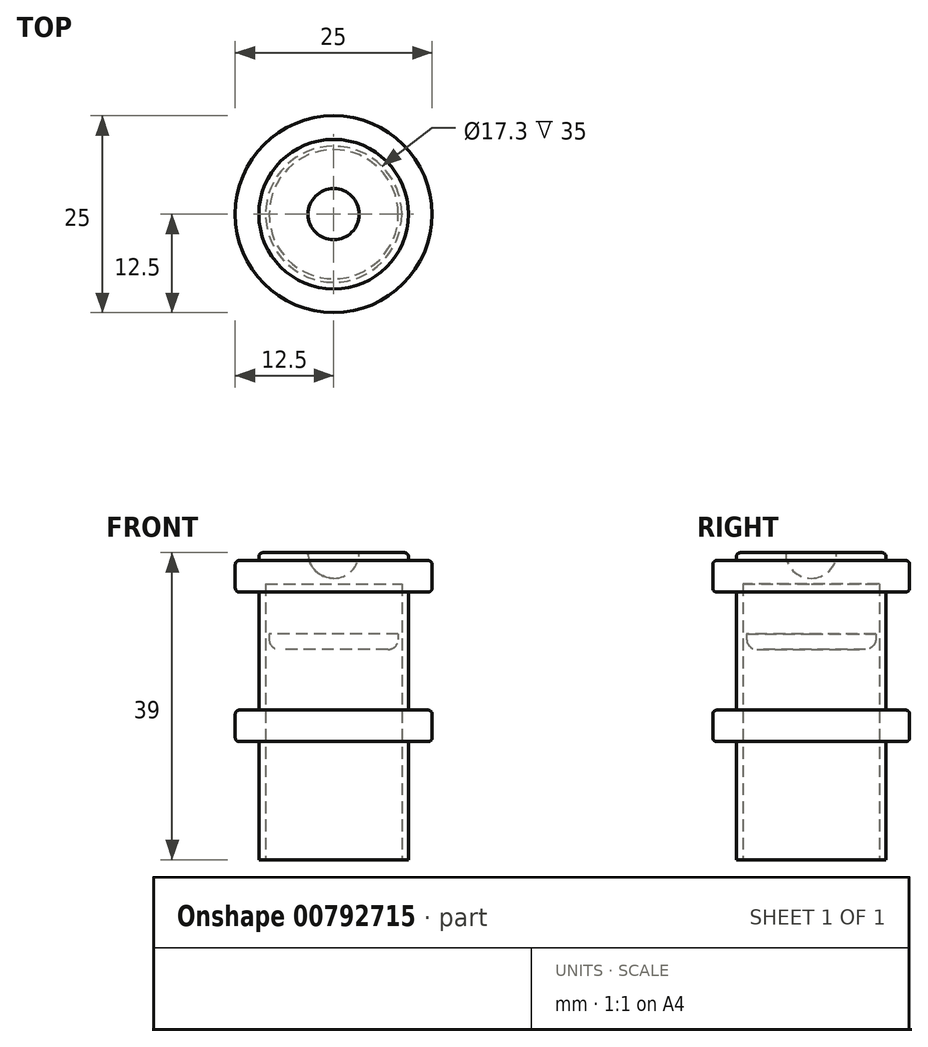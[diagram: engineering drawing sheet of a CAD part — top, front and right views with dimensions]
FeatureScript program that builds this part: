
annotation { "Feature Type Name" : "Feature", "Feature Type Description" : "" }
export const myFeature = defineFeature(function(context is Context, id is Id, definition is map)
    precondition{}
    {
        {
            var Q0;
            Q0=qCreatedBy(makeId("Front.planeOp"),FACE);
            var sketch = newSketch(context, id + "F0", { "sketchPlane" : qUnion([Q0])});
            skLineSegment(sketch, "E0", {"start": v(0, 0) * mm, "end": v(-9.5, 0) * mm});
            skLineSegment(sketch, "E1", {"start": v(-9.5, 0) * mm, "end": v(-9.5, 15) * mm});
            skLineSegment(sketch, "E2", {"start": v(-9.5, 15) * mm, "end": v(-12, 15) * mm});
            skLineSegment(sketch, "E3", {"start": v(-12.5, 15.5) * mm, "end": v(-12.5, 18.5) * mm});
            skLineSegment(sketch, "E4", {"start": v(-12, 19) * mm, "end": v(-9.5, 19) * mm});
            skLineSegment(sketch, "E5", {"start": v(-9.5, 19) * mm, "end": v(-9.5, 34) * mm});
            skLineSegment(sketch, "E6", {"start": v(-9.5, 34) * mm, "end": v(-12, 34) * mm});
            skLineSegment(sketch, "E7", {"start": v(-12.5, 34.5) * mm, "end": v(-12.5, 37.5) * mm});
            skLineSegment(sketch, "E8", {"start": v(-12, 38) * mm, "end": v(-9.5, 38) * mm});
            skLineSegment(sketch, "E9", {"start": v(-9.5, 38) * mm, "end": v(-9.5, 38.5) * mm});
            skLineSegment(sketch, "E10", {"start": v(-9, 39) * mm, "end": v(0, 39) * mm});
            skLineSegment(sketch, "E11", {"start": v(0, 39) * mm, "end": v(0, 0) * mm});
            skPoint(sketch, "E12.visualSharp", {"position": v(-12.5, 15) * mm});
            skArc(sketch, "E12.filletArc", {"start": v(-12.5, 15.5) * mm, "mid": v(-12.35, 15.15) * mm, "end": v(-12, 15) * mm});
            skPoint(sketch, "E13.visualSharp", {"position": v(-12.5, 19) * mm});
            skArc(sketch, "E13.filletArc", {"start": v(-12, 19) * mm, "mid": v(-12.35, 18.85) * mm, "end": v(-12.5, 18.5) * mm});
            skPoint(sketch, "E14.visualSharp", {"position": v(-12.5, 38) * mm});
            skArc(sketch, "E14.filletArc", {"start": v(-12, 38) * mm, "mid": v(-12.35, 37.85) * mm, "end": v(-12.5, 37.5) * mm});
            skPoint(sketch, "E15.visualSharp", {"position": v(-12.5, 34) * mm});
            skArc(sketch, "E15.filletArc", {"start": v(-12.5, 34.5) * mm, "mid": v(-12.35, 34.15) * mm, "end": v(-12, 34) * mm});
            skPoint(sketch, "E16.visualSharp", {"position": v(-9.5, 39) * mm});
            skArc(sketch, "E16.filletArc", {"start": v(-9, 39) * mm, "mid": v(-9.35, 38.85) * mm, "end": v(-9.5, 38.5) * mm});
            skArc(sketch, "E17", {"start": v(0, 35.75) * mm, "mid": v(-2.3, 36.7) * mm, "end": v(-3.25, 39) * mm});
            skSolve(sketch);
        }
        {
            var Q0;
            Q0=makeQuery(id+"F0.imprint","IMPRINT",FACE,{"disambiguationData":[TD([[makeQuery(id+"F0.imprint","IMPRINT",EDGE,{"derivedFrom":sQuery(id+"F0.wireOp",EDGE,"E0")}),-1.0]])]});
            var Q1;
            Q1=sQuery(id+"F0.wireOp",EDGE,"E0");
            var Q2;
            Q2=sQuery(id+"F0.wireOp",EDGE,"E1");
            var Q3;
            Q3=sQuery(id+"F0.wireOp",EDGE,"E2");
            var Q4;
            Q4=sQuery(id+"F0.wireOp",EDGE,"E3");
            var Q5;
            Q5=sQuery(id+"F0.wireOp",EDGE,"E4");
            var Q6;
            Q6=sQuery(id+"F0.wireOp",EDGE,"E5");
            var Q7;
            Q7=sQuery(id+"F0.wireOp",EDGE,"E6");
            var Q8;
            Q8=sQuery(id+"F0.wireOp",EDGE,"E7");
            var Q9;
            Q9=sQuery(id+"F0.wireOp",EDGE,"E8");
            var Q10;
            Q10=sQuery(id+"F0.wireOp",EDGE,"E9");
            var Q11;
            Q11=sQuery(id+"F0.wireOp",EDGE,"E10");
            var Q12;
            Q12=sQuery(id+"F0.wireOp",EDGE,"E12.filletArc");
            var Q13;
            Q13=sQuery(id+"F0.wireOp",EDGE,"E13.filletArc");
            var Q14;
            Q14=sQuery(id+"F0.wireOp",EDGE,"E14.filletArc");
            var Q15;
            Q15=sQuery(id+"F0.wireOp",EDGE,"E15.filletArc");
            var Q16;
            Q16=sQuery(id+"F0.wireOp",EDGE,"E16.filletArc");
            var Q17;
            Q17=sQuery(id+"F0.wireOp",EDGE,"E11");
            var Q18;
            Q18=sQuery(id+"F0.wireOp",EDGE,"E11");
            revolve(context, id + "F1", {"surfaceOperationType" : NewSurfaceOperationType.NEW, "entities" : qUnion([Q0]), "surfaceEntities" : qUnion([Q1, Q2, Q3, Q4, Q5, Q6, Q7, Q8, Q9, Q10, Q11, Q12, Q13, Q14, Q15, Q16, Q17]), "axis" : qUnion([Q18]), "revolveType" : RevolveType.FULL});
        }
        {
            var Q0;
            Q0=makeQuery(id+"F1.opRevolve","SWEPT_FACE",FACE,{"disambiguationData":[OSD([sQuery(id+"F0.wireOp",EDGE,"E0")])]});
            var sketch = newSketch(context, id + "F2", { "sketchPlane" : qUnion([Q0])});
            skCircle(sketch, "E18", {"center": v(0, 0) * mm, "radius": 8.65 * mm});
            skSolve(sketch);
        }
        {
            var Q0;
            Q0=makeQuery(id+"F2.imprint","IMPRINT",FACE,{"disambiguationData":[TD([[makeQuery(id+"F2.imprint","IMPRINT",EDGE,{"derivedFrom":sQuery(id+"F2.wireOp",EDGE,"E18")}),1.0]])]});
            extrude(context, id + "F3", {"entities" : qUnion([Q0]), "operationType" : NewBodyOperationType.REMOVE, "oppositeDirection" : true, "depth" : 35 * mm, "offsetDistance" : 25 * mm});
        }
        {
            var Q0;
            Q0=qCreatedBy(makeId("Top.planeOp"),FACE);
            cPlane(context, id + "F4", {"entities" : qUnion([Q0]), "cplaneType" : CPlaneType.OFFSET, "offset" : 26.7 * mm, "width" : 150 * mm, "height" : 150 * mm});
        }
        {
            var Q0;
            Q0=qCreatedBy(id+"F4.planeOp",FACE);
            var sketch = newSketch(context, id + "F5", { "sketchPlane" : qUnion([Q0])});
            skCircle(sketch, "E19", {"center": v(0, 0) * mm, "radius": 8.2 * mm});
            skSolve(sketch);
        }
        {
            var Q0;
            Q0 = qSketchRegion(id + "F5", true);
            extrude(context, id + "F6", {"entities" : qUnion([Q0]), "depth" : 2 * mm, "offsetDistance" : 25 * mm});
        }
        {
            var Q0;
            Q0=makeQuery(id+"F6.opExtrude","CAP_EDGE",EDGE,{"disambiguationData":[OSD([sQuery(id+"F5.wireOp",EDGE,"E19")])],"isStart":true});
            fillet(context, id + "F7", {"entities" : qUnion([Q0]), "radius" : 1.3 * mm, "tangentPropagation" : true, "allowEdgeOverflow" : false});
        }
    });
